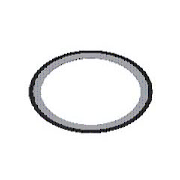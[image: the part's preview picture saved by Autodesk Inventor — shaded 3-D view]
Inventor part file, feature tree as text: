
AUTODESK INVENTOR PART (.ipt)
format: ipt  version: 2023.2 (Build 272271030, 271C)  size: 201,216 bytes
history: native  units: mm
features: other x4, revolve x2
ambient origin geometry x8: Origin, YZ Plane, XZ Plane, XY Plane, X Axis, Y Axis, Z Axis, Center Point
bodies: Solid1 (feature_tree)
feature tree (6):
  revolve  "Revolution1"  Angle=90.0deg
  revolve  "Revolution2"  [1 undecoded]
  other  "Work Point1"
  other  "Work Point2"
  other  "Work Axis1"
  other  "Work Axis2"
note: 1 required parameter value undecoded (feature->parameter linkage not recoverable at this tier; creation-order binding heuristic only, values carry confidence <= 0.55)
